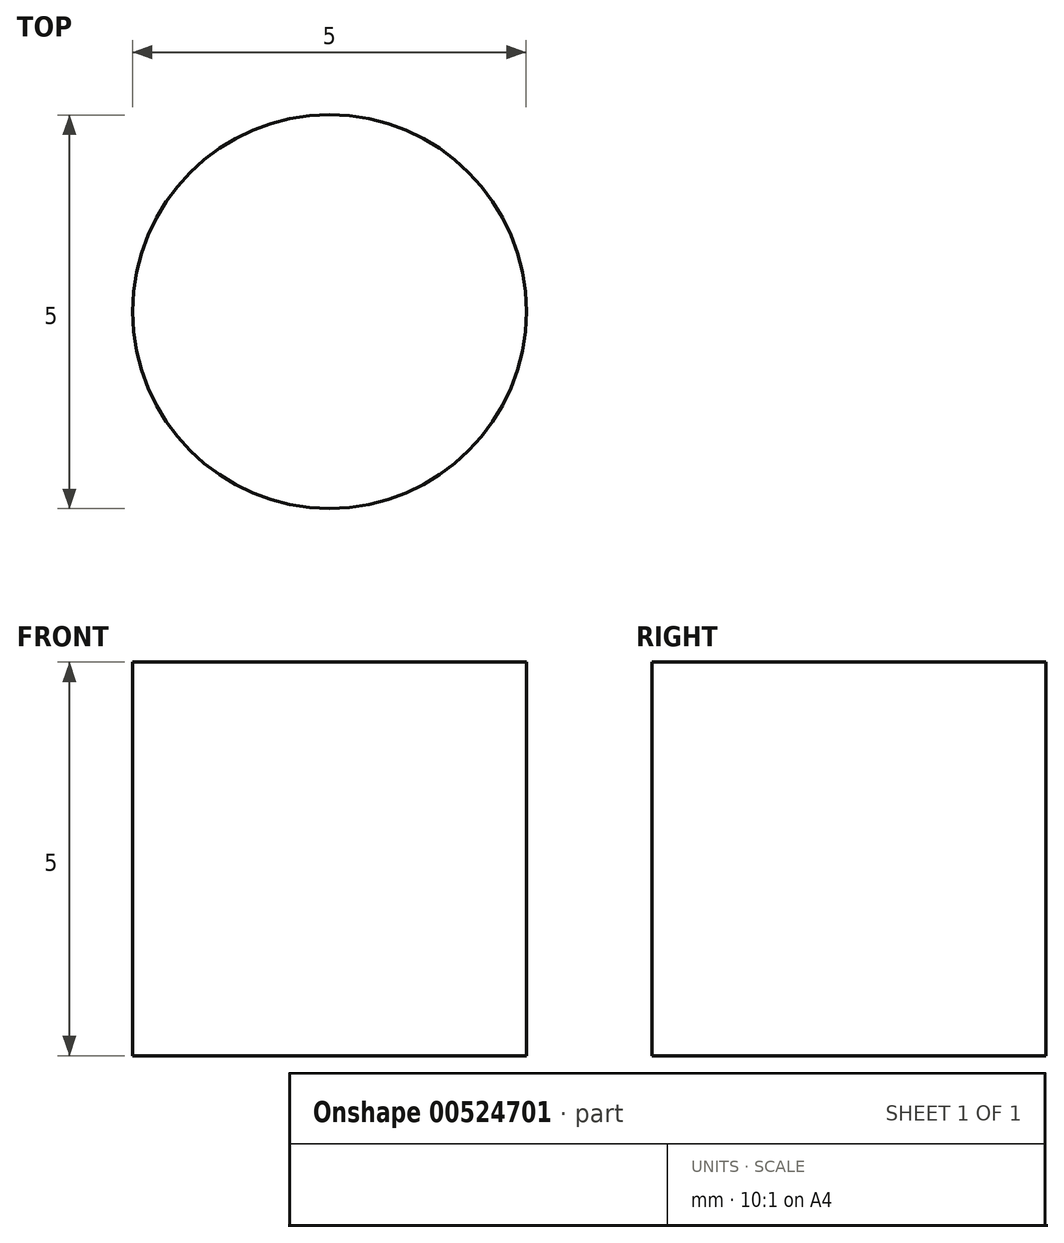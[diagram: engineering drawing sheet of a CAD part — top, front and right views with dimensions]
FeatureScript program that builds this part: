
annotation { "Feature Type Name" : "Feature", "Feature Type Description" : "" }
export const myFeature = defineFeature(function(context is Context, id is Id, definition is map)
    precondition{}
    {
        {
            var Q0;
            Q0=qCreatedBy(makeId("Top.planeOp"),FACE);
            var sketch = newSketch(context, id + "F0", { "sketchPlane" : qUnion([Q0])});
            skCircle(sketch, "E0", {"center": v(-18.1, -14.58) * mm, "radius": 2.5 * mm});
            skSolve(sketch);
        }
        {
            var Q0;
            Q0=makeQuery(id+"F0.imprint","IMPRINT",FACE,{"disambiguationData":[TD([[makeQuery(id+"F0.imprint","IMPRINT",EDGE,{"derivedFrom":sQuery(id+"F0.wireOp",EDGE,"E0")}),1.0]])]});
            extrude(context, id + "F1", {"entities" : qUnion([Q0]), "depth" : 5 * mm, "offsetDistance" : 25 * mm});
        }
    });
